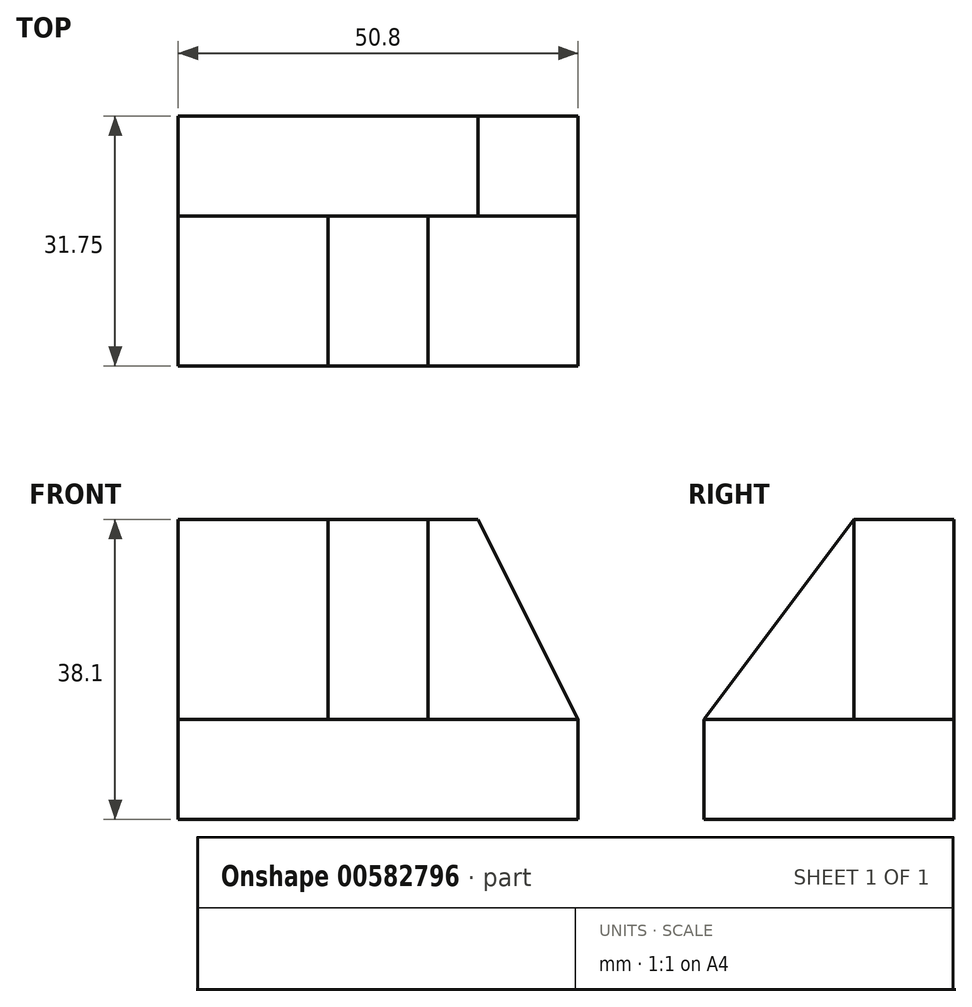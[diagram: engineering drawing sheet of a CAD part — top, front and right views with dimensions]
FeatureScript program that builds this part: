
annotation { "Feature Type Name" : "Feature", "Feature Type Description" : "" }
export const myFeature = defineFeature(function(context is Context, id is Id, definition is map)
    precondition{}
    {
        {
            var Q0;
            Q0=qCreatedBy(makeId("Front.planeOp"),FACE);
            var sketch = newSketch(context, id + "F0", { "sketchPlane" : qUnion([Q0])});
            skLineSegment(sketch, "E0", {"start": v(-58.29, 44.78) * mm, "end": v(-7.49, 44.78) * mm});
            skLineSegment(sketch, "E1", {"start": v(-7.49, 44.78) * mm, "end": v(-7.49, 6.68) * mm});
            skLineSegment(sketch, "E2", {"start": v(-7.49, 6.68) * mm, "end": v(-58.29, 6.68) * mm});
            skLineSegment(sketch, "E3", {"start": v(-58.29, 44.78) * mm, "end": v(-58.29, 6.68) * mm});
            skSolve(sketch);
        }
        {
            var Q0;
            Q0=makeQuery(id+"F0.imprint","IMPRINT",FACE,{"disambiguationData":[TD([[makeQuery(id+"F0.imprint","IMPRINT",EDGE,{"derivedFrom":sQuery(id+"F0.wireOp",EDGE,"E0")}),-1.0]])]});
            extrude(context, id + "F1", {"entities" : qUnion([Q0]), "depth" : 31.75 * mm, "offsetDistance" : 25.4 * mm});
        }
        {
            var Q0;
            Q0=makeQuery(id+"F1.opExtrude","CAP_FACE",FACE,{"disambiguationData":[OSD([sQuery(id+"F0.wireOp",EDGE,"E0"),sQuery(id+"F0.wireOp",EDGE,"E1"),sQuery(id+"F0.wireOp",EDGE,"E2"),sQuery(id+"F0.wireOp",EDGE,"E3")])],"isStart":true});
            var sketch = newSketch(context, id + "F2", { "sketchPlane" : qUnion([Q0])});
            skLineSegment(sketch, "E4", {"start": v(20.19, 44.78) * mm, "end": v(7.49, 19.38) * mm});
            skSolve(sketch);
        }
        {
            var Q0;
            Q0 = qSketchRegion(id + "F2", true);
            var Q1;
            {var subQ0=sQuery(id+"F2.wireOp",EDGE,"E4");Q1=makeQuery(id+"F2.imprint","IMPRINT",FACE,{"disambiguationData":[TD([[makeQuery(id+"F2.imprint","IMPRINT",EDGE,{"derivedFrom":subQ0}),-1.0]])]});}
            extrude(context, id + "F3", {"entities" : qUnion([Q0, Q1]), "operationType" : NewBodyOperationType.REMOVE, "oppositeDirection" : true, "depth" : 12.7 * mm, "offsetDistance" : 25.4 * mm});
        }
        {
            var Q0;
            Q0=makeQuery(id+"F1.opExtrude","SWEPT_FACE",FACE,{"disambiguationData":[OSD([sQuery(id+"F0.wireOp",EDGE,"E1")])]});
            var sketch = newSketch(context, id + "F4", { "sketchPlane" : qUnion([Q0])});
            skLineSegment(sketch, "E5", {"start": v(-12.7, 19.38) * mm, "end": v(-31.75, 19.38) * mm});
            skSolve(sketch);
        }
        {
            var Q0;
            Q0 = qSketchRegion(id + "F4", true);
            var Q1;
            {var subQ0=sQuery(id+"F4.wireOp",EDGE,"E5");Q1=makeQuery(id+"F4.imprint","IMPRINT",FACE,{"disambiguationData":[TD([[makeQuery(id+"F4.imprint","IMPRINT",EDGE,{"derivedFrom":subQ0}),-1.0]])]});}
            extrude(context, id + "F5", {"entities" : qUnion([Q0, Q1]), "operationType" : NewBodyOperationType.REMOVE, "oppositeDirection" : true, "depth" : 19.05 * mm, "offsetDistance" : 25.4 * mm});
        }
        {
            var Q0;
            Q0=makeQuery(id+"F5.boolean.opBoolean","COPY",FACE,{"derivedFrom":makeQuery(id+"F5.opExtrude","CAP_FACE",FACE,{"disambiguationData":[OSD([sQuery(id+"F0.wireOp",EDGE,"E0"),sQuery(id+"F0.wireOp",EDGE,"E1"),sQuery(id+"F4.wireOp",EDGE,"E5")])],"isStart":false})});
            var sketch = newSketch(context, id + "F6", { "sketchPlane" : qUnion([Q0])});
            skLineSegment(sketch, "E6", {"start": v(-12.7, 44.78) * mm, "end": v(-31.75, 19.38) * mm});
            skSolve(sketch);
        }
        {
            var Q0;
            Q0 = qSketchRegion(id + "F6", true);
            var Q1;
            Q1=makeQuery(id+"F6.imprint","IMPRINT",FACE,{"disambiguationData":[TD([[makeQuery(id+"F6.imprint","IMPRINT",EDGE,{"derivedFrom":sQuery(id+"F6.wireOp",EDGE,"E6")}),-1.0]])]});
            extrude(context, id + "F7", {"entities" : qUnion([Q0, Q1]), "operationType" : NewBodyOperationType.REMOVE, "oppositeDirection" : true, "depth" : 12.7 * mm, "offsetDistance" : 25.4 * mm});
        }
        {
            var Q0;
            Q0=makeQuery(id+"F1.opExtrude","CAP_FACE",FACE,{"disambiguationData":[OSD([sQuery(id+"F0.wireOp",EDGE,"E0"),sQuery(id+"F0.wireOp",EDGE,"E1"),sQuery(id+"F0.wireOp",EDGE,"E2"),sQuery(id+"F0.wireOp",EDGE,"E3")])],"isStart":false});
            var sketch = newSketch(context, id + "F8", { "sketchPlane" : qUnion([Q0])});
            skLineSegment(sketch, "E7", {"start": v(-39.24, 19.38) * mm, "end": v(-58.29, 19.38) * mm});
            skSolve(sketch);
        }
        {
            var Q0;
            Q0 = qSketchRegion(id + "F8", true);
            var Q1;
            {var subQ0=sQuery(id+"F8.wireOp",EDGE,"E7");Q1=makeQuery(id+"F8.imprint","IMPRINT",FACE,{"disambiguationData":[TD([[makeQuery(id+"F8.imprint","IMPRINT",EDGE,{"derivedFrom":subQ0}),-1.0]])]});}
            extrude(context, id + "F9", {"entities" : qUnion([Q0, Q1]), "operationType" : NewBodyOperationType.REMOVE, "oppositeDirection" : true, "depth" : 19.05 * mm, "offsetDistance" : 25.4 * mm});
        }
    });
